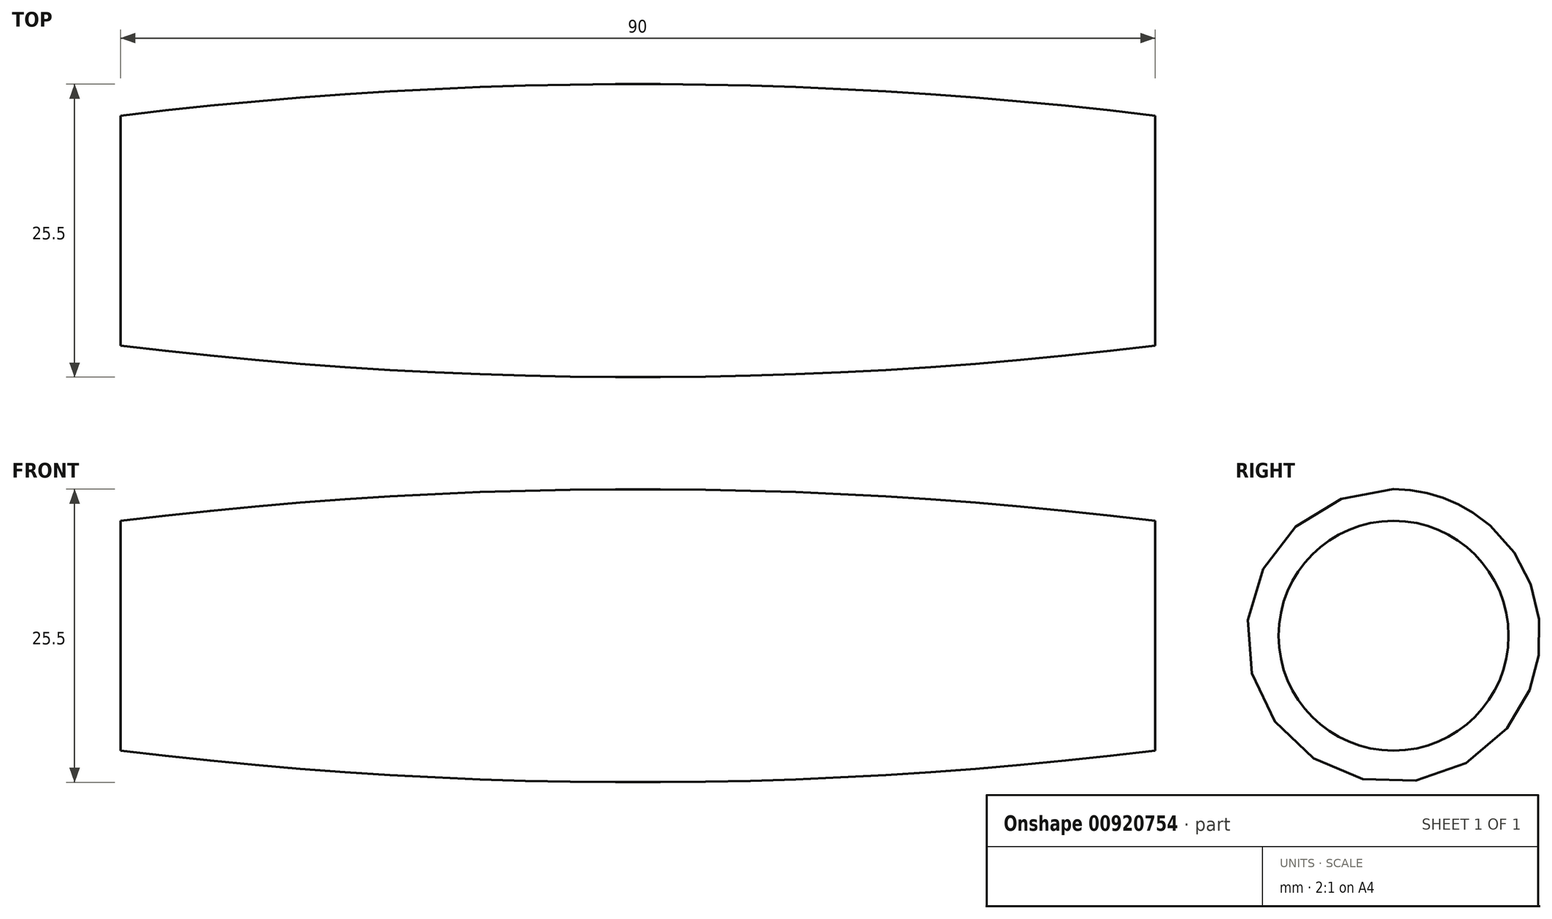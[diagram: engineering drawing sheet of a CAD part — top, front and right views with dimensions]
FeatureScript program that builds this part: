
annotation { "Feature Type Name" : "Feature", "Feature Type Description" : "" }
export const myFeature = defineFeature(function(context is Context, id is Id, definition is map)
    precondition{}
    {
        {
            var Q0;
            Q0=qCreatedBy(makeId("Top.planeOp"),FACE);
            var sketch = newSketch(context, id + "F0", { "sketchPlane" : qUnion([Q0])});
            skLineSegment(sketch, "E0", {"start": v(0, 0) * mm, "end": v(0, 10) * mm});
            skLineSegment(sketch, "E1", {"start": v(0, 0) * mm, "end": v(90, 0) * mm});
            skLineSegment(sketch, "E2", {"start": v(90, 0) * mm, "end": v(90, 10) * mm});
            skLineSegment(sketch, "E3", {"start": v(0, 0) * mm, "end": v(45, 0) * mm});
            skLineSegment(sketch, "E4", {"start": v(45, 0) * mm, "end": v(45, 12.75) * mm});
            skArc(sketch, "E5", {"start": v(90, 10) * mm, "mid": v(45, 12.75) * mm, "end": v(0, 10) * mm});
            skSolve(sketch);
        }
        {
            var Q0;
            Q0=makeQuery(id+"F0.imprint","IMPRINT",FACE,{"disambiguationData":[TD([[makeQuery(id+"F0.imprint","IMPRINT",EDGE,{"derivedFrom":sQuery(id+"F0.wireOp",EDGE,"E1")}),1.0]])]});
            var Q1;
            {var subQ0=sQuery(id+"F0.wireOp",EDGE,"E0");Q1=makeQuery(id+"F0.imprint","IMPRINT",FACE,{"disambiguationData":[TD([[makeQuery(id+"F0.imprint","IMPRINT",EDGE,{"derivedFrom":subQ0}),-1.0]])]});}
            var Q2;
            Q2=sQuery(id+"F0.wireOp",EDGE,"E1");
            revolve(context, id + "F1", {"surfaceOperationType" : NewSurfaceOperationType.NEW, "entities" : qUnion([Q0, Q1]), "axis" : qUnion([Q2]), "revolveType" : RevolveType.FULL});
        }
    });
